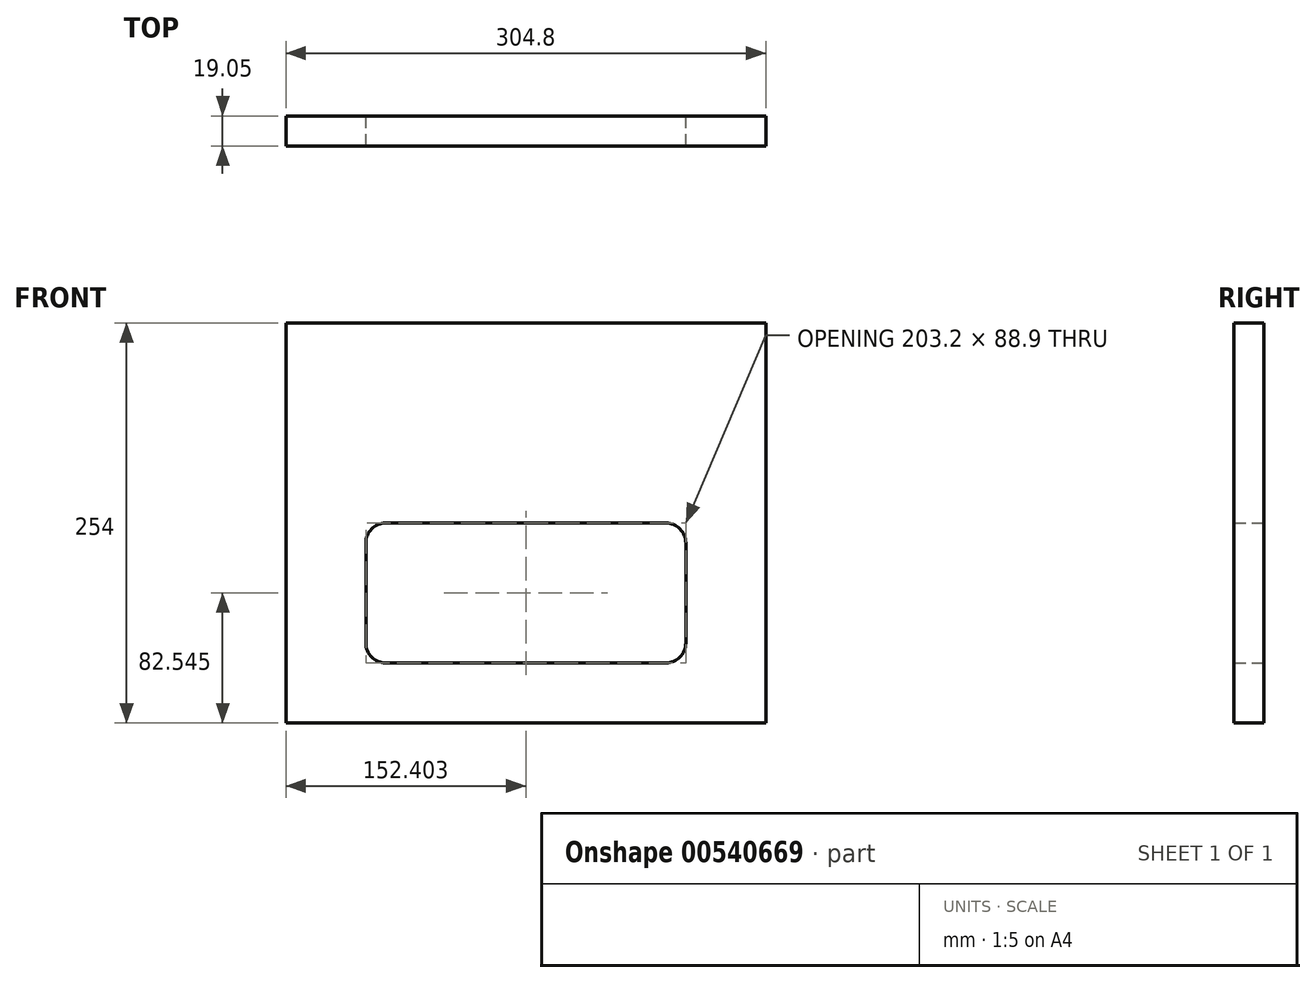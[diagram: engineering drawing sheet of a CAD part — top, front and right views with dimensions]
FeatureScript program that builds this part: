
annotation { "Feature Type Name" : "Feature", "Feature Type Description" : "" }
export const myFeature = defineFeature(function(context is Context, id is Id, definition is map)
    precondition{}
    {
        {
            var Q0;
            Q0=qCreatedBy(makeId("Front.planeOp"),FACE);
            var sketch = newSketch(context, id + "F0", { "sketchPlane" : qUnion([Q0])});
            skLineSegment(sketch, "E0.bottom", {"start": v(-422.17, 153.6) * mm, "end": v(-117.37, 153.6) * mm});
            skLineSegment(sketch, "E0.top", {"start": v(-422.17, -100.4) * mm, "end": v(-117.37, -100.4) * mm});
            skLineSegment(sketch, "E0.left", {"start": v(-422.17, 153.6) * mm, "end": v(-422.17, -100.4) * mm});
            skLineSegment(sketch, "E0.right", {"start": v(-117.37, 153.6) * mm, "end": v(-117.37, -100.4) * mm});
            skLineSegment(sketch, "E1.bottom", {"start": v(-358.67, 26.6) * mm, "end": v(-180.87, 26.6) * mm});
            skLineSegment(sketch, "E1.top", {"start": v(-358.67, -62.3) * mm, "end": v(-180.87, -62.3) * mm});
            skLineSegment(sketch, "E1.left", {"start": v(-371.37, 13.9) * mm, "end": v(-371.37, -49.6) * mm});
            skLineSegment(sketch, "E1.right", {"start": v(-168.17, 13.9) * mm, "end": v(-168.17, -49.6) * mm});
            skPoint(sketch, "E2.visualSharp", {"position": v(-371.37, 26.6) * mm});
            skArc(sketch, "E2.filletArc", {"start": v(-358.67, 26.6) * mm, "mid": v(-367.65, 22.89) * mm, "end": v(-371.37, 13.9) * mm});
            skPoint(sketch, "E3.visualSharp", {"position": v(-168.17, 26.6) * mm});
            skArc(sketch, "E3.filletArc", {"start": v(-168.17, 13.9) * mm, "mid": v(-171.89, 22.89) * mm, "end": v(-180.87, 26.6) * mm});
            skPoint(sketch, "E4.visualSharp", {"position": v(-168.17, -62.3) * mm});
            skArc(sketch, "E4.filletArc", {"start": v(-180.87, -62.3) * mm, "mid": v(-171.89, -58.58) * mm, "end": v(-168.17, -49.6) * mm});
            skPoint(sketch, "E5.visualSharp", {"position": v(-371.37, -62.3) * mm});
            skArc(sketch, "E5.filletArc", {"start": v(-371.37, -49.6) * mm, "mid": v(-367.65, -58.58) * mm, "end": v(-358.67, -62.3) * mm});
            skPoint(sketch, "E6", {"position": v(-168.17, -17.84) * mm});
            skPoint(sketch, "E7", {"position": v(-117.37, -17.84) * mm});
            skPoint(sketch, "E8", {"position": v(-269.77, 153.6) * mm});
            skPoint(sketch, "E9", {"position": v(-269.77, 26.6) * mm});
            skPoint(sketch, "E10", {"position": v(-269.77, -62.3) * mm});
            skPoint(sketch, "E11", {"position": v(-269.77, -100.4) * mm});
            skPoint(sketch, "E12", {"position": v(-371.37, -17.84) * mm});
            skPoint(sketch, "E13", {"position": v(-422.17, -17.84) * mm});
            skSolve(sketch);
        }
        {
            var Q0;
            Q0=makeQuery(id+"F0.imprint","IMPRINT",FACE,{"disambiguationData":[TD([[makeQuery(id+"F0.imprint","IMPRINT",EDGE,{"derivedFrom":sQuery(id+"F0.wireOp",EDGE,"E0.bottom")}),-1.0]])]});
            extrude(context, id + "F1", {"entities" : qUnion([Q0]), "depth" : 19.05 * mm, "offsetDistance" : 25.4 * mm});
        }
    });
